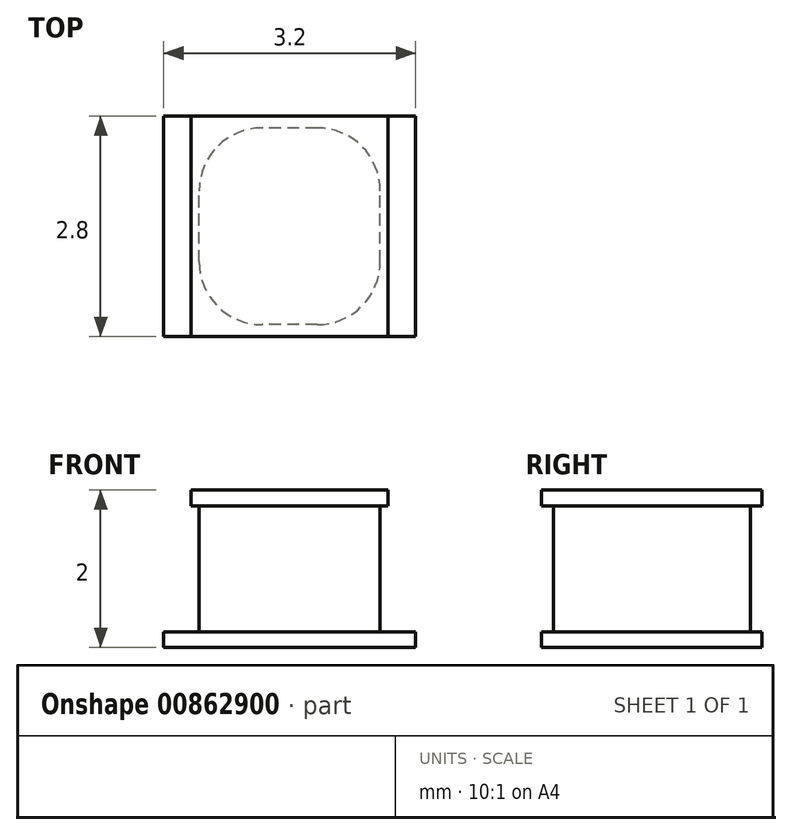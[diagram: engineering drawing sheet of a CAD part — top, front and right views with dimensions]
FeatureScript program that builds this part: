
annotation { "Feature Type Name" : "Feature", "Feature Type Description" : "" }
export const myFeature = defineFeature(function(context is Context, id is Id, definition is map)
    precondition{}
    {
        {
            var Q0;
            Q0=qCreatedBy(makeId("Top.planeOp"),FACE);
            var sketch = newSketch(context, id + "F0", { "sketchPlane" : qUnion([Q0])});
            skLineSegment(sketch, "E0.bottom", {"start": v(1.6, -1.4) * mm, "end": v(-1.6, -1.4) * mm});
            skLineSegment(sketch, "E0.top", {"start": v(1.6, 1.4) * mm, "end": v(-1.6, 1.4) * mm});
            skLineSegment(sketch, "E0.left", {"start": v(1.6, -1.4) * mm, "end": v(1.6, 1.4) * mm});
            skLineSegment(sketch, "E0.right", {"start": v(-1.6, -1.4) * mm, "end": v(-1.6, 1.4) * mm});
            skPoint(sketch, "E0.middle", {"position": v(0, 0) * mm});
            skSolve(sketch);
        }
        {
            var Q0;
            Q0=makeQuery(id+"F0.imprint","IMPRINT",FACE,{"disambiguationData":[TD([[makeQuery(id+"F0.imprint","IMPRINT",EDGE,{"derivedFrom":sQuery(id+"F0.wireOp",EDGE,"E0.bottom")}),-1.0]])]});
            extrude(context, id + "F1", {"entities" : qUnion([Q0]), "depth" : 0.2 * mm, "offsetDistance" : 25 * mm});
        }
        {
            var Q0;
            Q0=makeQuery(id+"F1.opExtrude","CAP_FACE",FACE,{"disambiguationData":[OSD([sQuery(id+"F0.wireOp",EDGE,"E0.bottom"),sQuery(id+"F0.wireOp",EDGE,"E0.top"),sQuery(id+"F0.wireOp",EDGE,"E0.left"),sQuery(id+"F0.wireOp",EDGE,"E0.right")])],"isStart":false});
            var sketch = newSketch(context, id + "F2", { "sketchPlane" : qUnion([Q0])});
            skLineSegment(sketch, "E1.bottom", {"start": v(1.15, -1.25) * mm, "end": v(-1.15, -1.25) * mm});
            skLineSegment(sketch, "E1.top", {"start": v(1.15, 1.25) * mm, "end": v(-1.15, 1.25) * mm});
            skLineSegment(sketch, "E1.left", {"start": v(1.15, -1.25) * mm, "end": v(1.15, 1.25) * mm});
            skLineSegment(sketch, "E1.right", {"start": v(-1.15, -1.25) * mm, "end": v(-1.15, 1.25) * mm});
            skPoint(sketch, "E1.middle", {"position": v(0, 0) * mm});
            skSolve(sketch);
        }
        {
            var Q0;
            Q0=makeQuery(id+"F2.imprint","IMPRINT",FACE,{"disambiguationData":[TD([[makeQuery(id+"F2.imprint","IMPRINT",EDGE,{"derivedFrom":sQuery(id+"F2.wireOp",EDGE,"E1.bottom")}),-1.0]])]});
            extrude(context, id + "F3", {"entities" : qUnion([Q0]), "depth" : 1.6 * mm, "offsetDistance" : 25 * mm});
        }
        {
            var Q0;
            Q0=makeQuery(id+"F3.opExtrude","CAP_FACE",FACE,{"disambiguationData":[OSD([sQuery(id+"F2.wireOp",EDGE,"E1.bottom"),sQuery(id+"F2.wireOp",EDGE,"E1.top"),sQuery(id+"F2.wireOp",EDGE,"E1.left"),sQuery(id+"F2.wireOp",EDGE,"E1.right")])],"isStart":false});
            var sketch = newSketch(context, id + "F4", { "sketchPlane" : qUnion([Q0])});
            skLineSegment(sketch, "E2.bottom", {"start": v(1.25, -1.4) * mm, "end": v(-1.25, -1.4) * mm});
            skLineSegment(sketch, "E2.top", {"start": v(1.25, 1.4) * mm, "end": v(-1.25, 1.4) * mm});
            skLineSegment(sketch, "E2.left", {"start": v(1.25, -1.4) * mm, "end": v(1.25, 1.4) * mm});
            skLineSegment(sketch, "E2.right", {"start": v(-1.25, -1.4) * mm, "end": v(-1.25, 1.4) * mm});
            skPoint(sketch, "E2.middle", {"position": v(0, 0) * mm});
            skSolve(sketch);
        }
        {
            var Q0;
            Q0=makeQuery(id+"F4.imprint","IMPRINT",FACE,{"disambiguationData":[TD([[makeQuery(id+"F4.imprint","IMPRINT",EDGE,{"derivedFrom":makeQuery(id+"F3.opExtrude","CAP_EDGE",EDGE,{"disambiguationData":[OSD([sQuery(id+"F2.wireOp",EDGE,"E1.bottom")])],"isStart":false})}),-1.0]])]});
            var Q1;
            Q1=makeQuery(id+"F4.imprint","IMPRINT",FACE,{"disambiguationData":[TD([[makeQuery(id+"F4.imprint","IMPRINT",EDGE,{"derivedFrom":sQuery(id+"F4.wireOp",EDGE,"E2.bottom")}),-1.0]])]});
            extrude(context, id + "F5", {"entities" : qUnion([Q0, Q1]), "depth" : 0.2 * mm, "offsetDistance" : 25 * mm});
        }
        {
            var Q0;
            Q0=makeQuery(id+"F3.opExtrude","SWEPT_EDGE",EDGE,{"disambiguationData":[OSD([sQuery(id+"F2.wireOp",EDGE,"E1.bottom"),sQuery(id+"F2.wireOp",EDGE,"E1.right")])]});
            var Q1;
            Q1=makeQuery(id+"F3.opExtrude","SWEPT_EDGE",EDGE,{"disambiguationData":[OSD([sQuery(id+"F2.wireOp",EDGE,"E1.bottom"),sQuery(id+"F2.wireOp",EDGE,"E1.left")])]});
            var Q2;
            Q2=makeQuery(id+"F3.opExtrude","SWEPT_EDGE",EDGE,{"disambiguationData":[OSD([sQuery(id+"F2.wireOp",EDGE,"E1.top"),sQuery(id+"F2.wireOp",EDGE,"E1.left")])]});
            var Q3;
            Q3=makeQuery(id+"F3.opExtrude","SWEPT_EDGE",EDGE,{"disambiguationData":[OSD([sQuery(id+"F2.wireOp",EDGE,"E1.top"),sQuery(id+"F2.wireOp",EDGE,"E1.right")])]});
            fillet(context, id + "F6", {"entities" : qUnion([Q0, Q1, Q2, Q3]), "radius" : 0.8 * mm, "tangentPropagation" : true, "allowEdgeOverflow" : false});
        }
    });
